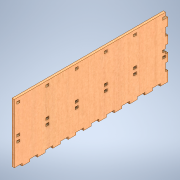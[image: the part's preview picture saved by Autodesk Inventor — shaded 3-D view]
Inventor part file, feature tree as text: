
AUTODESK INVENTOR PART (.ipt)
format: ipt  version: 2021 (Build 250183000, 183)  size: 312,832 bytes
history: native  units: mm
features: extrude x4, sketch x4, other x1
ambient origin geometry x8: Origin, YZ Plane, XZ Plane, XY Plane, X Axis, Y Axis, Z Axis, Center Point
bodies: Solid1 (feature_tree)
feature tree (9):
  other  "DoosjeRechter-Linkerkant"
  extrude  "Extrusion1"  Depth=200.0mm
  extrude  "Extrusion2"  Depth=100.0mm
  extrude  "Extrusion3"  Depth=3.0mm TaperAngle=0.0deg
  extrude  "Extrusion4"  Depth=3.0mm TaperAngle=0.0deg
  sketch  "Sketch1"  dims[d0=77.0mm d1=200.0mm]
  sketch  "Sketch2"  dims[d2=3.0mm d3=0.0mm d7=100.0mm d9=20.0mm d10=10.0mm d12=10.0mm]
  sketch  "Sketch3"  dims[d25=10.0mm d26=3.0mm d27=0.0mm]
  sketch  "Sketch4"  dims[d28=10.0mm d29=3.0mm d30=10.0mm d31=20.0mm d32=3.0mm d33=0.0mm d34=4.0mm d35=3.0mm d36=60.0mm d38=38.0mm d39=20.0mm d41=37.0mm d44=0.0mm d45=0.0mm d46=60.0mm d48=38.0mm d49=20.0mm d51=7.0mm d54=4.0mm]
